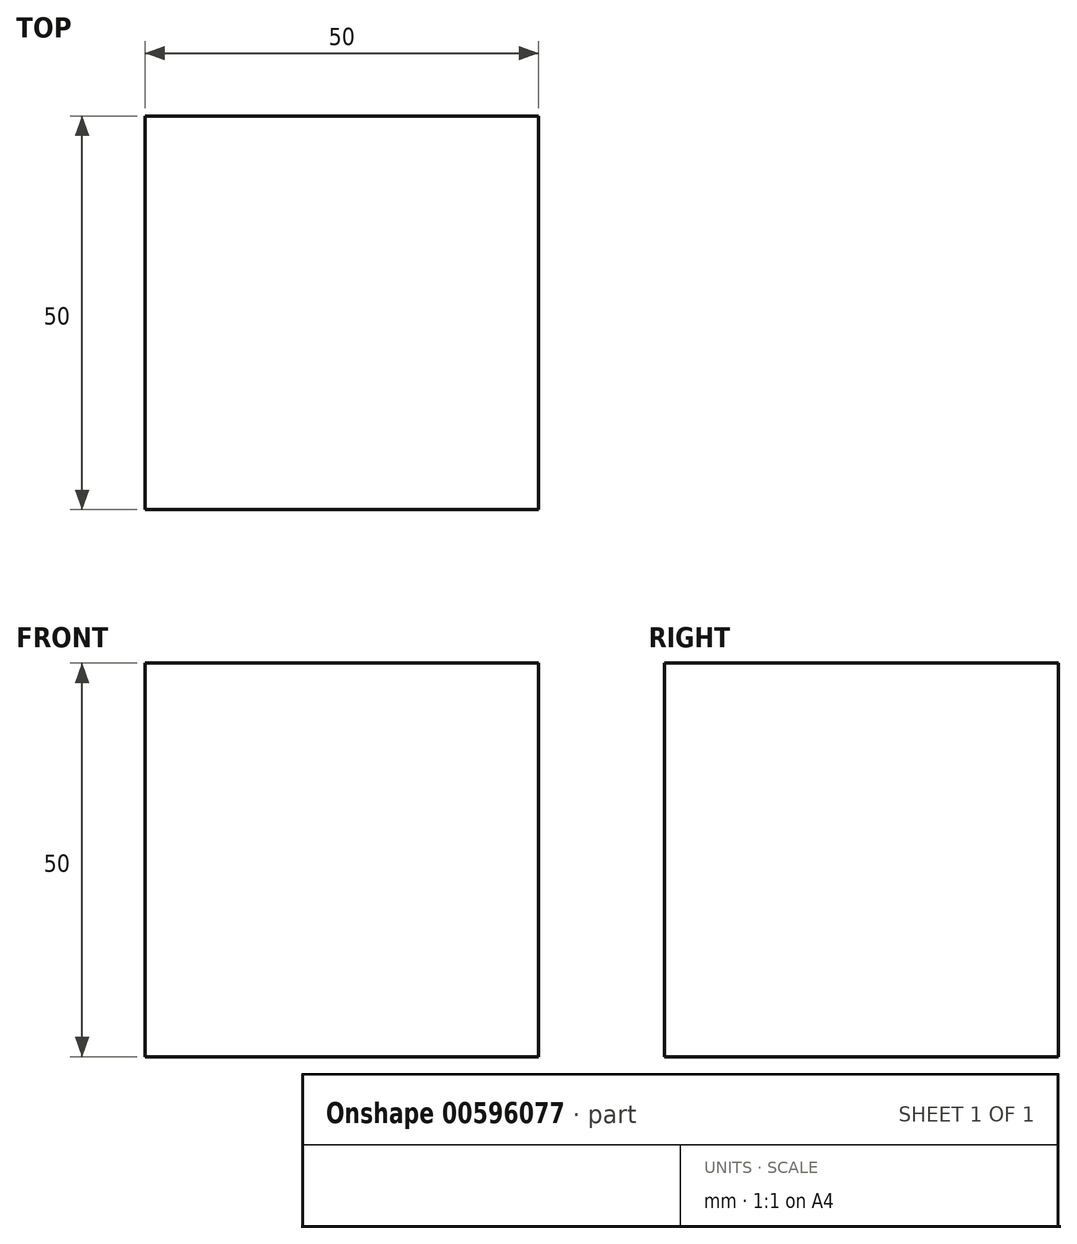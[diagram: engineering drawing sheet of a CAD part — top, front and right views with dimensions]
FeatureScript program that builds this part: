
annotation { "Feature Type Name" : "Feature", "Feature Type Description" : "" }
export const myFeature = defineFeature(function(context is Context, id is Id, definition is map)
    precondition{}
    {
        {
            var Q0;
            Q0=qCreatedBy(makeId("Top.planeOp"),FACE);
            var sketch = newSketch(context, id + "F0", { "sketchPlane" : qUnion([Q0])});
            skLineSegment(sketch, "E0.bottom", {"start": v(27.51, 25) * mm, "end": v(-22.49, 25) * mm});
            skLineSegment(sketch, "E0.top", {"start": v(27.51, -25) * mm, "end": v(-22.49, -25) * mm});
            skLineSegment(sketch, "E0.left", {"start": v(27.51, 25) * mm, "end": v(27.51, -25) * mm});
            skLineSegment(sketch, "E0.right", {"start": v(-22.49, 25) * mm, "end": v(-22.49, -25) * mm});
            skPoint(sketch, "E0.middle", {"position": v(2.51, 0) * mm});
            skSolve(sketch);
        }
        {
            var Q0;
            Q0 = qSketchRegion(id + "F0", true);
            extrude(context, id + "F1", {"entities" : qUnion([Q0]), "depth" : 50 * mm, "offsetDistance" : 25 * mm});
        }
    });
